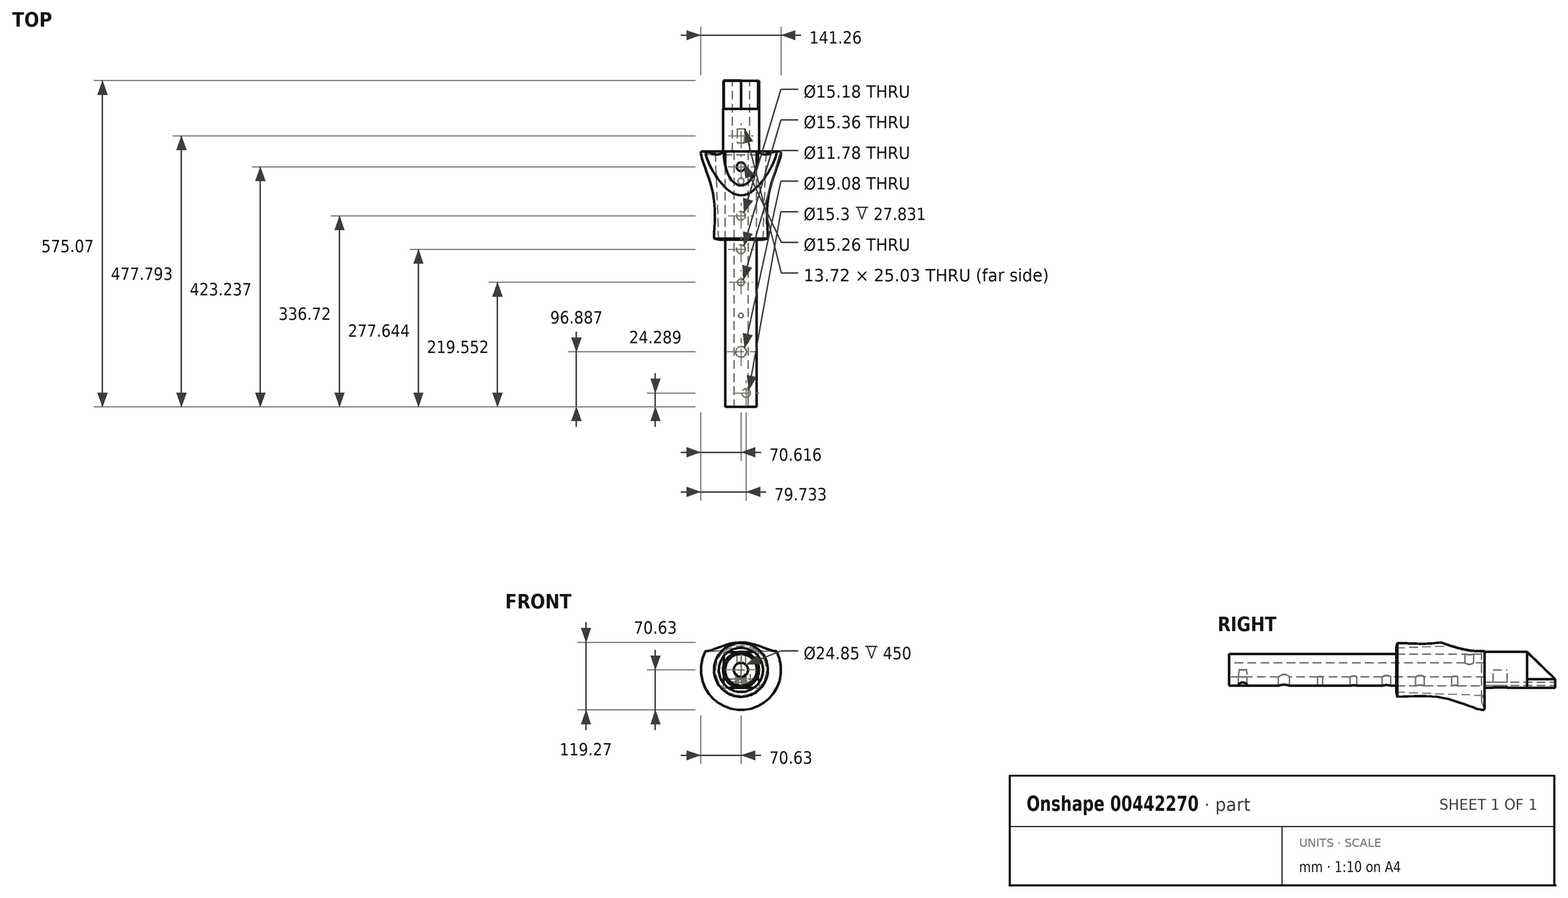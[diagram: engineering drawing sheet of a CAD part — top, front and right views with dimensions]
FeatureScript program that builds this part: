
annotation { "Feature Type Name" : "Feature", "Feature Type Description" : "" }
export const myFeature = defineFeature(function(context is Context, id is Id, definition is map)
    precondition{}
    {
        {
            var Q0;
            Q0=qCreatedBy(makeId("Front.planeOp"),FACE);
            var sketch = newSketch(context, id + "F0", { "sketchPlane" : qUnion([Q0])});
            skCircle(sketch, "E0", {"center": v(0, 0) * mm, "radius": 27.87 * mm});
            skSolve(sketch);
        }
        {
            var Q0;
            Q0 = qSketchRegion(id + "F0", true);
            extrude(context, id + "F1", {"entities" : qUnion([Q0]), "depth" : 450 * mm});
        }
        {
            var Q0;
            Q0=makeQuery(id+"F1.opExtrude","CAP_FACE",FACE,{"disambiguationData":[OSD([sQuery(id+"F0.wireOp",EDGE,"E0")])],"isStart":false});
            var sketch = newSketch(context, id + "F2", { "sketchPlane" : qUnion([Q0])});
            skCircle(sketch, "E1", {"center": v(0, 0) * mm, "radius": 12.43 * mm});
            skSolve(sketch);
        }
        {
            var Q0;
            Q0=qCreatedBy(makeId("Front.planeOp"),FACE);
            var sketch = newSketch(context, id + "F3", { "sketchPlane" : qUnion([Q0])});
            skCircle(sketch, "E2", {"center": v(0, 0) * mm, "radius": 31.74 * mm});
            skSolve(sketch);
        }
        {
            var Q0;
            Q0 = qSketchRegion(id + "F3", true);
            extrude(context, id + "F4", {"entities" : qUnion([Q0]), "operationType" : NewBodyOperationType.ADD, "oppositeDirection" : true, "depth" : 75 * mm});
        }
        {
            var Q0;
            Q0=qCreatedBy(makeId("Top.planeOp"),FACE);
            var sketch = newSketch(context, id + "F5", { "sketchPlane" : qUnion([Q0])});
            skCircle(sketch, "E3", {"center": v(0, -52.07) * mm, "radius": 5.46 * mm});
            skSolve(sketch);
        }
        {
            var Q0;
            Q0 = qSketchRegion(id + "F5", true);
            extrude(context, id + "F6", {"entities" : qUnion([Q0]), "operationType" : NewBodyOperationType.REMOVE, "endBound" : BoundingType.THROUGH_ALL, "oppositeDirection" : true, "depth" : 25 * mm});
        }
        {
            var Q0;
            Q0 = qSketchRegion(id + "F2", true);
            var Q1;
            Q1=makeQuery(id+"F4.opExtrude","CAP_FACE",FACE,{"disambiguationData":[OSD([sQuery(id+"F3.wireOp",EDGE,"E2")])],"isStart":true});
            extrude(context, id + "F7", {"entities" : qUnion([Q0]), "operationType" : NewBodyOperationType.REMOVE, "endBound" : BoundingType.UP_TO_SURFACE, "oppositeDirection" : true, "endBoundEntityFace" : qUnion([Q1]), "depth" : 450 * mm});
        }
        {
            var Q0;
            Q0=qCreatedBy(makeId("Top.planeOp"),FACE);
            var sketch = newSketch(context, id + "F8", { "sketchPlane" : qUnion([Q0])});
            skCircle(sketch, "E4", {"center": v(0, -113.28) * mm, "radius": 7.59 * mm});
            skSolve(sketch);
        }
        {
            var Q0;
            Q0 = qSketchRegion(id + "F8", true);
            extrude(context, id + "F9", {"entities" : qUnion([Q0]), "operationType" : NewBodyOperationType.REMOVE, "endBound" : BoundingType.THROUGH_ALL, "oppositeDirection" : true, "depth" : 25 * mm});
        }
        {
            var Q0;
            Q0=qCreatedBy(makeId("Top.planeOp"),FACE);
            var sketch = newSketch(context, id + "F10", { "sketchPlane" : qUnion([Q0])});
            skCircle(sketch, "E5", {"center": v(0, -172.36) * mm, "radius": 7.68 * mm});
            skSolve(sketch);
        }
        {
            var Q0;
            Q0 = qSketchRegion(id + "F10", true);
            extrude(context, id + "F11", {"entities" : qUnion([Q0]), "operationType" : NewBodyOperationType.REMOVE, "endBound" : BoundingType.THROUGH_ALL, "oppositeDirection" : true, "depth" : 25 * mm});
        }
        {
            var Q0;
            Q0=qCreatedBy(makeId("Top.planeOp"),FACE);
            var sketch = newSketch(context, id + "F12", { "sketchPlane" : qUnion([Q0])});
            skCircle(sketch, "E6", {"center": v(0, -230.45) * mm, "radius": 5.9 * mm});
            skSolve(sketch);
        }
        {
            var Q0;
            Q0 = qSketchRegion(id + "F12", true);
            extrude(context, id + "F13", {"entities" : qUnion([Q0]), "operationType" : NewBodyOperationType.REMOVE, "endBound" : BoundingType.THROUGH_ALL, "oppositeDirection" : true, "depth" : 25 * mm});
        }
        {
            var Q0;
            Q0=qCreatedBy(makeId("Top.planeOp"),FACE);
            var sketch = newSketch(context, id + "F14", { "sketchPlane" : qUnion([Q0])});
            skCircle(sketch, "E7", {"center": v(0, -289.2) * mm, "radius": 4.23 * mm});
            skSolve(sketch);
        }
        {
            var Q0;
            Q0 = qSketchRegion(id + "F14", true);
            extrude(context, id + "F15", {"entities" : qUnion([Q0]), "operationType" : NewBodyOperationType.REMOVE, "endBound" : BoundingType.THROUGH_ALL, "oppositeDirection" : true, "depth" : 25 * mm});
        }
        {
            var Q0;
            Q0=qCreatedBy(makeId("Top.planeOp"),FACE);
            var sketch = newSketch(context, id + "F16", { "sketchPlane" : qUnion([Q0])});
            skCircle(sketch, "E8", {"center": v(0, -353.11) * mm, "radius": 9.54 * mm});
            skSolve(sketch);
        }
        {
            var Q0;
            Q0 = qSketchRegion(id + "F16", true);
            extrude(context, id + "F17", {"entities" : qUnion([Q0]), "operationType" : NewBodyOperationType.REMOVE, "endBound" : BoundingType.THROUGH_ALL, "oppositeDirection" : true, "depth" : 25 * mm});
        }
        {
            var Q0;
            Q0=qCreatedBy(makeId("Top.planeOp"),FACE);
            var sketch = newSketch(context, id + "F18", { "sketchPlane" : qUnion([Q0])});
            skCircle(sketch, "E9", {"center": v(9.1, -425.71) * mm, "radius": 7.65 * mm});
            skSolve(sketch);
        }
        {
            var Q0;
            Q0 = qSketchRegion(id + "F18", true);
            extrude(context, id + "F19", {"entities" : qUnion([Q0]), "operationType" : NewBodyOperationType.REMOVE, "endBound" : BoundingType.THROUGH_ALL, "oppositeDirection" : true, "depth" : 25 * mm});
        }
        {
            var Q0;
            Q0=qCreatedBy(makeId("Top.planeOp"),FACE);
            var sketch = newSketch(context, id + "F20", { "sketchPlane" : qUnion([Q0])});
            skLineSegment(sketch, "E10.bottom", {"start": v(-6.87, 15.28) * mm, "end": v(6.85, 15.28) * mm});
            skLineSegment(sketch, "E10.top", {"start": v(-6.87, 40.3) * mm, "end": v(6.85, 40.3) * mm});
            skLineSegment(sketch, "E10.left", {"start": v(-6.87, 15.28) * mm, "end": v(-6.87, 40.3) * mm});
            skLineSegment(sketch, "E10.right", {"start": v(6.85, 15.28) * mm, "end": v(6.85, 40.3) * mm});
            skSolve(sketch);
        }
        {
            var Q0;
            Q0 = qSketchRegion(id + "F20", true);
            extrude(context, id + "F21", {"entities" : qUnion([Q0]), "operationType" : NewBodyOperationType.REMOVE, "endBound" : BoundingType.THROUGH_ALL, "oppositeDirection" : true, "depth" : 25 * mm});
        }
        {
            var Q0;
            Q0=makeQuery(id+"F4.opExtrude","CAP_FACE",FACE,{"disambiguationData":[OSD([sQuery(id+"F3.wireOp",EDGE,"E2")])],"isStart":false});
            var sketch = newSketch(context, id + "F22", { "sketchPlane" : qUnion([Q0])});
            skLineSegment(sketch, "E11", {"start": v(-31.74, -16.27) * mm, "end": v(-31.74, -31.74) * mm});
            skLineSegment(sketch, "E12", {"start": v(0, -31.74) * mm, "end": v(-31.74, -31.74) * mm});
            skLineSegment(sketch, "E13.bottom", {"start": v(-31.74, -31.74) * mm, "end": v(30.74, -31.74) * mm});
            skLineSegment(sketch, "E13.top", {"start": v(-31.74, -16.27) * mm, "end": v(30.74, -16.27) * mm});
            skLineSegment(sketch, "E13.left", {"start": v(-31.74, -31.74) * mm, "end": v(-31.74, -16.27) * mm});
            skLineSegment(sketch, "E13.right", {"start": v(30.74, -31.74) * mm, "end": v(30.74, -16.27) * mm});
            skPoint(sketch, "E14.orphan", {"position": v(-31.74, 0) * mm});
            skSolve(sketch);
        }
        {
            var Q0;
            Q0 = qSketchRegion(id + "F22", true);
            extrude(context, id + "F23", {"entities" : qUnion([Q0]), "operationType" : NewBodyOperationType.ADD, "depth" : 50 * mm});
        }
        {
            var Q0;
            Q0=makeQuery(id+"F23.opExtrude","CAP_FACE",FACE,{"disambiguationData":[OSD([sQuery(id+"F22.wireOp",EDGE,"E13.bottom"),sQuery(id+"F22.wireOp",EDGE,"E13.top"),sQuery(id+"F22.wireOp",EDGE,"E13.left"),sQuery(id+"F22.wireOp",EDGE,"E13.right")])],"isStart":false});
            var sketch = newSketch(context, id + "F24", { "sketchPlane" : qUnion([Q0])});
            skLineSegment(sketch, "E15.bottom", {"start": v(-15.44, -21.36) * mm, "end": v(14.87, -21.36) * mm});
            skLineSegment(sketch, "E15.top", {"start": v(-15.44, -27.15) * mm, "end": v(14.87, -27.15) * mm});
            skLineSegment(sketch, "E15.left", {"start": v(-15.44, -21.36) * mm, "end": v(-15.44, -27.15) * mm});
            skLineSegment(sketch, "E15.right", {"start": v(14.87, -21.36) * mm, "end": v(14.87, -27.15) * mm});
            skSolve(sketch);
        }
        {
            var Q0;
            Q0 = qSketchRegion(id + "F24", true);
            var Q1;
            Q1=qCreatedBy(makeId("Front.planeOp"),FACE);
            extrude(context, id + "F25", {"entities" : qUnion([Q0]), "operationType" : NewBodyOperationType.REMOVE, "endBound" : BoundingType.UP_TO_SURFACE, "oppositeDirection" : true, "endBoundEntityFace" : qUnion([Q1]), "depth" : 25 * mm});
        }
        {
            var Q0;
            Q0=qCreatedBy(makeId("Top.planeOp"),FACE);
            var sketch = newSketch(context, id + "F26", { "sketchPlane" : qUnion([Q0])});
            skCircle(sketch, "E16", {"center": v(0, -26.76) * mm, "radius": 7.63 * mm});
            skSolve(sketch);
        }
        {
            var Q0;
            Q0 = qSketchRegion(id + "F26", true);
            extrude(context, id + "F27", {"entities" : qUnion([Q0]), "operationType" : NewBodyOperationType.REMOVE, "endBound" : BoundingType.THROUGH_ALL, "depth" : 25 * mm});
        }
        {
            var Q0;
            Q0=qCreatedBy(makeId("Right.planeOp"),FACE);
            var sketch = newSketch(context, id + "F28", { "sketchPlane" : qUnion([Q0])});
            skFitSpline(sketch, "E17", {"points": [v(0, -44.93) * mm, v(0, -69.13) * mm, v(-60.26, -52.47) * mm, v(-153.73, -47.45) * mm], "startDerivative": vector(-163.03, -106.34) * mm, "endDerivative": vector(-253.27, -8.14) * mm});
            skLineSegment(sketch, "E18", {"start": v(0, -44.93) * mm, "end": v(-155.38, -38.88) * mm});
            skLineSegment(sketch, "E19", {"start": v(-153.73, -47.45) * mm, "end": v(-155.38, -38.88) * mm});
            skSolve(sketch);
        }
        {
            var Q0;
            Q0=makeQuery(id+"F28.imprint","IMPRINT",FACE,{"disambiguationData":[TD([[makeQuery(id+"F28.imprint","IMPRINT",EDGE,{"derivedFrom":sQuery(id+"F28.wireOp",EDGE,"E17")}),-1.0]])]});
            var Q1;
            Q1=makeQuery(id+"F4.opExtrude","CAP_EDGE",EDGE,{"disambiguationData":[OSD([sQuery(id+"F3.wireOp",EDGE,"E2")])],"isStart":true});
            sweep(context, id + "F29", {"profiles" : qUnion([Q0]), "path" : qUnion([Q1])});
        }
        {
            var Q0;
            Q0=qCreatedBy(makeId("Right.planeOp"),FACE);
            var sketch = newSketch(context, id + "F30", { "sketchPlane" : qUnion([Q0])});
            skFitSpline(sketch, "E20", {"points": [v(39.2, 45.61) * mm, v(-25.66, 34.2) * mm, v(-138.61, 85.52) * mm, v(-118.66, 99.42) * mm, v(12.83, 100.49) * mm], "startDerivative": vector(-228.11, -104.53) * mm, "endDerivative": vector(471.42, -23.84) * mm});
            skLineSegment(sketch, "E21", {"start": v(12.83, 100.49) * mm, "end": v(39.2, 45.61) * mm});
            skSolve(sketch);
        }
        {
            var Q0;
            Q0 = qSketchRegion(id + "F30", true);
            extrude(context, id + "F31", {"entities" : qUnion([Q0]), "operationType" : NewBodyOperationType.REMOVE, "endBound" : BoundingType.THROUGH_ALL, "oppositeDirection" : true, "depth" : 25 * mm, "hasSecondDirection" : true, "secondDirectionBound" : SecondDirectionBoundingType.THROUGH_ALL, "secondDirectionOppositeDirection" : false, "secondDirectionDepth" : 25 * mm});
        }
        {
            var Q0;
            Q0=qCreatedBy(makeId("Right.planeOp"),FACE);
            var sketch = newSketch(context, id + "F32", { "sketchPlane" : qUnion([Q0])});
            skLineSegment(sketch, "E22", {"start": v(75.06, 31.54) * mm, "end": v(75.06, -16.35) * mm});
            skLineSegment(sketch, "E23", {"start": v(75.06, -16.35) * mm, "end": v(124.89, -16.35) * mm});
            skLineSegment(sketch, "E24", {"start": v(75.06, 31.54) * mm, "end": v(124.89, -16.35) * mm});
            skSolve(sketch);
        }
        {
            var Q0;
            Q0 = qSketchRegion(id + "F32", true);
            extrude(context, id + "F33", {"entities" : qUnion([Q0]), "operationType" : NewBodyOperationType.ADD, "depth" : 30 * mm});
        }
        {
            var Q0;
            Q0=qCreatedBy(makeId("Right.planeOp"),FACE);
            var sketch = newSketch(context, id + "F34", { "sketchPlane" : qUnion([Q0])});
            skLineSegment(sketch, "E25", {"start": v(75.16, 31.5) * mm, "end": v(75.16, -16.45) * mm});
            skLineSegment(sketch, "E26", {"start": v(75.16, -16.45) * mm, "end": v(125.07, -16.45) * mm});
            skLineSegment(sketch, "E27", {"start": v(125.07, -16.45) * mm, "end": v(75.16, 31.5) * mm});
            skSolve(sketch);
        }
        {
            var Q0;
            Q0 = qSketchRegion(id + "F34", true);
            extrude(context, id + "F35", {"entities" : qUnion([Q0]), "operationType" : NewBodyOperationType.ADD, "oppositeDirection" : true, "depth" : 30 * mm});
        }
    });
